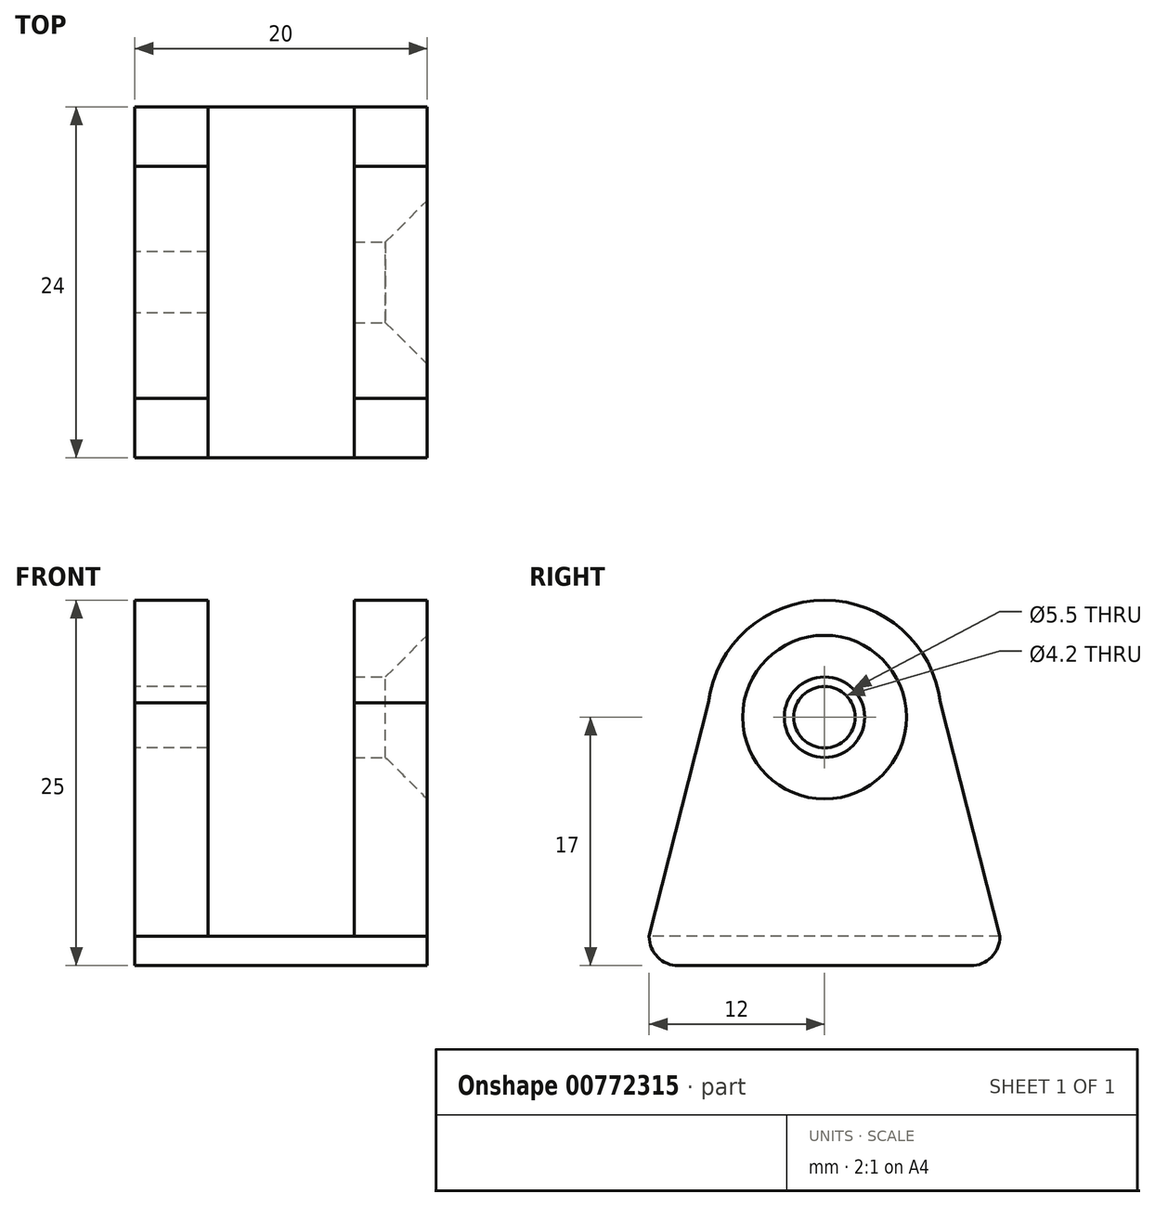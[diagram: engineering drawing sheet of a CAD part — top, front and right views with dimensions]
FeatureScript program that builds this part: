
annotation { "Feature Type Name" : "Feature", "Feature Type Description" : "" }
export const myFeature = defineFeature(function(context is Context, id is Id, definition is map)
    precondition{}
    {
        {
            var Q0;
            Q0=qCreatedBy(makeId("Top.planeOp"),FACE);
            var sketch = newSketch(context, id + "F0", { "sketchPlane" : qUnion([Q0])});
            skLineSegment(sketch, "E0.bottom", {"start": v(0, 0) * mm, "end": v(20, 0) * mm});
            skLineSegment(sketch, "E0.top", {"start": v(0, 24) * mm, "end": v(20, 24) * mm});
            skLineSegment(sketch, "E0.left", {"start": v(0, 0) * mm, "end": v(0, 24) * mm});
            skLineSegment(sketch, "E0.right", {"start": v(20, 0) * mm, "end": v(20, 24) * mm});
            skSolve(sketch);
        }
        {
            var Q0;
            Q0=makeQuery(id+"F0.imprint","IMPRINT",FACE,{"disambiguationData":[TD([[makeQuery(id+"F0.imprint","IMPRINT",EDGE,{"derivedFrom":sQuery(id+"F0.wireOp",EDGE,"E0.bottom")}),1.0]])]});
            extrude(context, id + "F1", {"entities" : qUnion([Q0]), "depth" : 25 * mm, "offsetDistance" : 25 * mm});
        }
        {
            var Q0;
            Q0=makeQuery(id+"F1.opExtrude","SWEPT_FACE",FACE,{"disambiguationData":[OSD([sQuery(id+"F0.wireOp",EDGE,"E0.bottom")])]});
            var sketch = newSketch(context, id + "F2", { "sketchPlane" : qUnion([Q0])});
            skPoint(sketch, "E1", {"position": v(5, 2) * mm});
            skPoint(sketch, "E2", {"position": v(15, 2) * mm});
            skLineSegment(sketch, "E3", {"start": v(5, 2) * mm, "end": v(5, 25) * mm});
            skLineSegment(sketch, "E4", {"start": v(5, 25) * mm, "end": v(15, 25) * mm});
            skLineSegment(sketch, "E5", {"start": v(15, 25) * mm, "end": v(15, 2) * mm});
            skLineSegment(sketch, "E6", {"start": v(5, 2) * mm, "end": v(15, 2) * mm});
            skSolve(sketch);
        }
        {
            var Q0;
            Q0=makeQuery(id+"F2.imprint","IMPRINT",FACE,{"disambiguationData":[TD([[makeQuery(id+"F2.imprint","IMPRINT",EDGE,{"derivedFrom":sQuery(id+"F2.wireOp",EDGE,"E3")}),-1.0]])]});
            extrude(context, id + "F3", {"entities" : qUnion([Q0]), "operationType" : NewBodyOperationType.REMOVE, "oppositeDirection" : true, "depth" : 25 * mm, "offsetDistance" : 25 * mm});
        }
        {
            var Q0;
            Q0=makeQuery(id+"F1.opExtrude","SWEPT_FACE",FACE,{"disambiguationData":[OSD([sQuery(id+"F0.wireOp",EDGE,"E0.right")])]});
            var sketch = newSketch(context, id + "F4", { "sketchPlane" : qUnion([Q0])});
            skPoint(sketch, "E7", {"position": v(12, 17) * mm});
            skPoint(sketch, "E7.positionSnap0", {"position": v(12, 25) * mm});
            skArc(sketch, "E8", {"start": v(19.94, 17.97) * mm, "mid": v(12, 25) * mm, "end": v(4.06, 17.97) * mm});
            skPoint(sketch, "E9", {"position": v(0, 2) * mm});
            skLineSegment(sketch, "E10", {"start": v(3.75, 17) * mm, "end": v(4, 17) * mm});
            skLineSegment(sketch, "E11", {"start": v(0, 2) * mm, "end": v(4.06, 17.97) * mm});
            skLineSegment(sketch, "E12", {"start": v(19.94, 17.97) * mm, "end": v(24, 2) * mm});
            skSolve(sketch);
        }
        {
            var Q0;
            {var subQ0=sQuery(id+"F4.wireOp",EDGE,"E11");var subQ3=sQuery(id+"F4.wireOp",EDGE,"E10");var subQ5=makeQuery(id+"F4.imprint","INTERSECT",VERTEX,{"derivedFrom":[subQ3,subQ0]});Q0=makeQuery(id+"F4.imprint","IMPRINT",FACE,{"disambiguationData":[TD([[makeQuery(id+"F4.imprint","IMPRINT",EDGE,{"disambiguationData":[TD([[subQ5,-1.0]])],"derivedFrom":subQ3}),1.0]])]});}
            var Q1;
            {var subQ3=sQuery(id+"F4.wireOp",EDGE,"UP6nhRDy-AZdy-ySFw-T1Sy-Gd9mO86kPvoG");Q1=makeQuery(id+"F4.imprint","IMPRINT",FACE,{"disambiguationData":[TD([[makeQuery(id+"F4.imprint","IMPRINT",EDGE,{"derivedFrom":subQ3}),-1.0]])]});}
            var Q2;
            {var subQ0=sQuery(id+"F0.wireOp",EDGE,"E0.right");var subQ1=makeQuery(id+"F1.opExtrude","CAP_EDGE",EDGE,{"disambiguationData":[OSD([subQ0])],"isStart":false});var subQ6=sQuery(id+"F4.wireOp",EDGE,"E8");var subQ8=makeQuery(id+"F4.imprint","INTERSECT",VERTEX,{"derivedFrom":[subQ1,subQ6]});Q2=makeQuery(id+"F4.imprint","IMPRINT",FACE,{"disambiguationData":[TD([[makeQuery(id+"F4.imprint","IMPRINT",EDGE,{"disambiguationData":[TD([[subQ8,-1.0]])],"derivedFrom":subQ6}),-1.0]])]});}
            var Q3;
            {var subQ0=sQuery(id+"F4.wireOp",EDGE,"E12");Q3=makeQuery(id+"F4.imprint","IMPRINT",FACE,{"disambiguationData":[TD([[makeQuery(id+"F4.imprint","IMPRINT",EDGE,{"derivedFrom":subQ0}),1.0]])]});}
            extrude(context, id + "F5", {"entities" : qUnion([Q0, Q1, Q2, Q3]), "operationType" : NewBodyOperationType.REMOVE, "oppositeDirection" : true, "depth" : 25 * mm, "offsetDistance" : 25 * mm});
        }
        {
            var Q0;
            Q0=sQuery(id+"F4.wireOp",VERTEX,"E7");
            var Q1;
            Q1=makeQuery(id+"F1.opExtrude","SWEPT_BODY",BODY,{"disambiguationData":[OSD([sQuery(id+"F0.wireOp",EDGE,"E0.bottom"),sQuery(id+"F0.wireOp",EDGE,"E0.top"),sQuery(id+"F0.wireOp",EDGE,"E0.left"),sQuery(id+"F0.wireOp",EDGE,"E0.right")])]});
            hole(context, id + "F6", {"style" : HoleStyle.C_SINK, "endStyle" : HoleEndStyle.BLIND, "standardTappedOrClearance" : lookupTablePath({ "standard" : "ISO", "fit" : "Normal", "size" : "M5", "type" : "Clearance" }), "standardBlindInLast" : lookupTablePath({ "fit" : "Standard", "standard" : "ISO", "size" : "M5", "type" : "Clearance" }), "holeDiameter" : 5.5 * mm, "cSinkDiameter" : 11.2 * mm, "cSinkAngle" : 90 * degree, "majorDiameter" : 5 * mm, "holeDepth" : 12.9 * mm, "isTappedThrough" : true, "tappedDepth" : 10.5 * mm, "tapClearance" : 3, "locations" : qUnion([Q0]), "scope" : qUnion([Q1])});
        }
        {
            var Q0;
            Q0=makeQuery(id+"F1.opExtrude","SWEPT_FACE",FACE,{"disambiguationData":[OSD([sQuery(id+"F0.wireOp",EDGE,"E0.left")])]});
            var sketch = newSketch(context, id + "F7", { "sketchPlane" : qUnion([Q0])});
            skPoint(sketch, "E13", {"position": v(-12, 17) * mm});
            skSolve(sketch);
        }
        {
            var Q0;
            Q0=sQuery(id+"F7.wireOp",VERTEX,"E13");
            var Q1;
            Q1=makeQuery(id+"F1.opExtrude","SWEPT_BODY",BODY,{"disambiguationData":[OSD([sQuery(id+"F0.wireOp",EDGE,"E0.bottom"),sQuery(id+"F0.wireOp",EDGE,"E0.top"),sQuery(id+"F0.wireOp",EDGE,"E0.left"),sQuery(id+"F0.wireOp",EDGE,"E0.right")])]});
            hole(context, id + "F8", {"style" : HoleStyle.SIMPLE, "endStyle" : HoleEndStyle.BLIND, "standardTappedOrClearance" : lookupTablePath({ "standard" : "ISO", "engagement" : "75%", "pitch" : "0.8 mm", "size" : "M5", "type" : "Tapped" }), "standardBlindInLast" : lookupTablePath({ "standard" : "ISO", "engagement" : "75%", "pitch" : "0.8 mm", "size" : "M5", "type" : "Tapped" }), "holeDiameter" : 4.2 * mm, "majorDiameter" : 5 * mm, "showTappedDepth" : true, "holeDepth" : 12.9 * mm, "isTappedThrough" : true, "tappedDepth" : 10.5 * mm, "tapClearance" : 3, "locations" : qUnion([Q0]), "scope" : qUnion([Q1])});
        }
        {
            var Q0;
            Q0=makeQuery(id+"F1.opExtrude","CAP_EDGE",EDGE,{"disambiguationData":[OSD([sQuery(id+"F0.wireOp",EDGE,"E0.top")])],"isStart":true});
            var Q1;
            Q1=makeQuery(id+"F1.opExtrude","CAP_EDGE",EDGE,{"disambiguationData":[OSD([sQuery(id+"F0.wireOp",EDGE,"E0.bottom")])],"isStart":true});
            fillet(context, id + "F9", {"entities" : qUnion([Q0, Q1]), "radius" : 2 * mm, "tangentPropagation" : true, "allowEdgeOverflow" : false});
        }
    });
